# Revit family: Flush_Valve_Cover_and_Flush_Valve-Whitehall-BestCare-WH2802-SLPT-ADA_Series
name_source: partatom
category: Plumbing Fixtures
units: mm (PartAtom-declared; Revit-internal decimal feet)

## family parameters
Cut with Voids When Loaded = No
Host = Face
OmniClass Number = 23.65.70.00
OmniClass Title = Terminals for Supplied Liquids and Gases
Part Type = Normal
Room Calculation Point = No
Round Connector Dimension = Use Diameter
Shared = Yes

## types (8) — shared parameters
ADA Compliant = Yes
Activation Button Type = Pushbutton
Assembly Code = D2020300
CW Connection = No
CWFU = 5
Depth = 5"
Description = BestCare® Ligature-Flush Valve Cover and Flush Valve
HW Connection = No
Installation Type = Wall Mounted
Manufacturer = Whitehall Mfg.
Product Documentation Link = https://www.whitehallmfg.com
Product Page URL = https://www.whitehallmfg.com
Tempered Water Connection = Yes
Tempered Water Connection Diameter = 1"
URL = https://www.whitehallmfg.com
Vent Connection = No
WFU = 5
Waste Connection = No
zero-valued in all types: HWFU

## per-type parameters (varying)
| type | Default Elevation | Family Type | Finish | Flush Rate | Height | Material | Width |
| WH2802-ADA-1.28 | 0" | TOILET WH2802-ADA Series : MWH2802-SLPT-SO-EG10-E525 | Stainless Steel-Whitehall-Enviro Glazed White | 1.28 GPF | 14 5/8" | Stainless Steel-Whitehall-Enviro Glazed White | 14" |
| WH2802-ADA-1.6 | 0" | TOILET WH2802-ADA Series : MWH2802-SLPT-SO-EG10-E525 | Stainless Steel-Whitehall-Enviro Glazed White | 1.6 GPF | 14 5/8" | Stainless Steel-Whitehall-Enviro Glazed White | 14" |
| WH2802-ADA-1.28-SS | 0" | TOILET WH2802-ADA Series : MWH2802-SLPT-SO-EG10-E525 | Metal-Whitehall-Stainless Steel | 1.28 GPF | 14 5/8" | Metal-Whitehall-Stainless Steel | 14" |
| WH2802-ADA-1.6-SS | 0" | TOILET WH2802-ADA Series : MWH2802-SLPT-SO-EG10-E525 | Metal-Whitehall-Stainless Steel | 1.6 GPF | 14 5/8" | Metal-Whitehall-Stainless Steel | 14" |
| WH2802-ADA-.125 | 0" | URINAL WH2802-ADA Series : MWH2802-SLPT-EG10-E518-2-Left | Stainless Steel-Whitehall-Enviro Glazed White | .125 GPF | 17 7/8" | Stainless Steel-Whitehall-Enviro Glazed White | 13" |
| WH2802-ADA-0.5 | 0" | URINAL WH2802-ADA Series : MWH2802-SLPT-EG10-E518-2-Left | Stainless Steel-Whitehall-Enviro Glazed White | 0.5 GPF | 17 7/8" | Stainless Steel-Whitehall-Enviro Glazed White | 13" |
| WH2802-ADA-.125-SS | 0" | URINAL WH2802-ADA Series : MWH2802-SLPT-EG10-E518-2-Left | Metal-Whitehall-Stainless Steel | .125 GPF | 17 7/8" | Metal-Whitehall-Stainless Steel | 13" |
| WH2802-ADA-0.5-SS | 1" | URINAL WH2802-ADA Series : MWH2802-SLPT-EG10-E518-2-Left | Metal-Whitehall-Stainless Steel | 0.5 GPF | 17 7/8" | Metal-Whitehall-Stainless Steel | 13" |

note: column(s) folded — value = type name in every type: Model

## geometry (parser evidence)
native form markers: Sweep x19
no freeform markers — native parametric forms only
